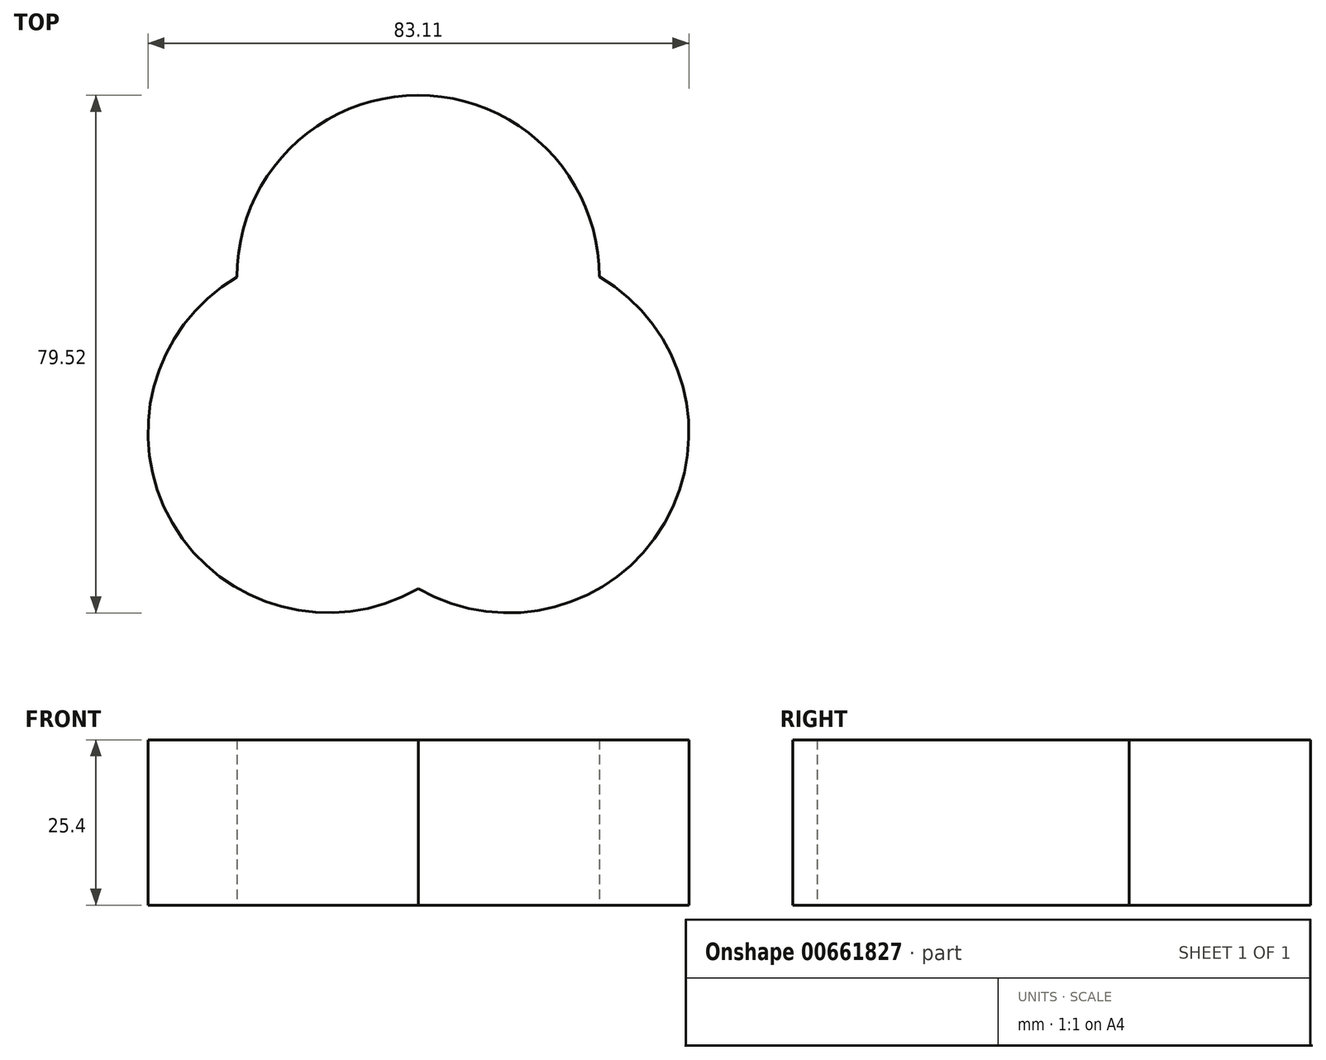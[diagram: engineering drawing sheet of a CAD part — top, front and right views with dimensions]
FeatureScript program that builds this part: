
annotation { "Feature Type Name" : "Feature", "Feature Type Description" : "" }
export const myFeature = defineFeature(function(context is Context, id is Id, definition is map)
    precondition{}
    {
        {
            var Q0;
            Q0=qCreatedBy(makeId("Top.planeOp"),FACE);
            var sketch = newSketch(context, id + "F0", { "sketchPlane" : qUnion([Q0])});
            skCircle(sketch, "E0", {"center": v(0, 0) * mm, "radius": 27.71 * mm});
            skCircle(sketch, "E1", {"center": v(-27.71, 0) * mm, "radius": 27.69 * mm});
            skCircle(sketch, "E2", {"center": v(-13.88, 23.99) * mm, "radius": 27.83 * mm});
            skSolve(sketch);
        }
        {
            var Q0;
            {var subQ0=sQuery(id+"F0.wireOp",EDGE,"E2");var subQ1=sQuery(id+"F0.wireOp",EDGE,"E0");var subQ2=makeQuery(id+"F0.imprint","INTERSECT",VERTEX,{"disambiguationData":[OD(0.0)],"derivedFrom":[subQ1,subQ0]});Q0=makeQuery(id+"F0.imprint","IMPRINT",FACE,{"disambiguationData":[TD([[makeQuery(id+"F0.imprint","IMPRINT",EDGE,{"disambiguationData":[TD([[subQ2,-1.0]])],"derivedFrom":subQ1}),-1.0]])]});}
            var Q1;
            {var subQ0=sQuery(id+"F0.wireOp",EDGE,"E1");var subQ1=sQuery(id+"F0.wireOp",EDGE,"E0");var subQ2=makeQuery(id+"F0.imprint","INTERSECT",VERTEX,{"disambiguationData":[OD(1.0)],"derivedFrom":[subQ1,subQ0]});Q1=makeQuery(id+"F0.imprint","IMPRINT",FACE,{"disambiguationData":[TD([[makeQuery(id+"F0.imprint","IMPRINT",EDGE,{"disambiguationData":[TD([[subQ2,-1.0]])],"derivedFrom":subQ1}),-1.0]])]});}
            var Q2;
            {var subQ0=sQuery(id+"F0.wireOp",EDGE,"E2");var subQ1=sQuery(id+"F0.wireOp",EDGE,"E0");var subQ2=makeQuery(id+"F0.imprint","INTERSECT",VERTEX,{"disambiguationData":[OD(0.0)],"derivedFrom":[subQ1,subQ0]});Q2=makeQuery(id+"F0.imprint","IMPRINT",FACE,{"disambiguationData":[TD([[makeQuery(id+"F0.imprint","IMPRINT",EDGE,{"disambiguationData":[TD([[subQ2,-1.0]])],"derivedFrom":subQ1}),1.0]])]});}
            var Q3;
            {var subQ0=sQuery(id+"F0.wireOp",EDGE,"E1");var subQ1=sQuery(id+"F0.wireOp",EDGE,"E0");var subQ2=makeQuery(id+"F0.imprint","INTERSECT",VERTEX,{"disambiguationData":[OD(1.0)],"derivedFrom":[subQ1,subQ0]});Q3=makeQuery(id+"F0.imprint","IMPRINT",FACE,{"disambiguationData":[TD([[makeQuery(id+"F0.imprint","IMPRINT",EDGE,{"disambiguationData":[TD([[subQ2,-1.0]])],"derivedFrom":subQ1}),1.0]])]});}
            var Q4;
            {var subQ0=sQuery(id+"F0.wireOp",EDGE,"E1");var subQ1=sQuery(id+"F0.wireOp",EDGE,"E0");var subQ2=makeQuery(id+"F0.imprint","INTERSECT",VERTEX,{"disambiguationData":[OD(0.0)],"derivedFrom":[subQ1,subQ0]});Q4=makeQuery(id+"F0.imprint","IMPRINT",FACE,{"disambiguationData":[TD([[makeQuery(id+"F0.imprint","IMPRINT",EDGE,{"disambiguationData":[TD([[subQ2,1.0]])],"derivedFrom":subQ1}),1.0]])]});}
            var Q5;
            {var subQ0=sQuery(id+"F0.wireOp",EDGE,"E2");var subQ1=sQuery(id+"F0.wireOp",EDGE,"E0");var subQ2=makeQuery(id+"F0.imprint","INTERSECT",VERTEX,{"disambiguationData":[OD(0.0)],"derivedFrom":[subQ1,subQ0]});Q5=makeQuery(id+"F0.imprint","IMPRINT",FACE,{"disambiguationData":[TD([[makeQuery(id+"F0.imprint","IMPRINT",EDGE,{"disambiguationData":[TD([[subQ2,1.0]])],"derivedFrom":subQ1}),1.0]])]});}
            var Q6;
            {var subQ0=sQuery(id+"F0.wireOp",EDGE,"E1");var subQ1=sQuery(id+"F0.wireOp",EDGE,"E0");var subQ2=makeQuery(id+"F0.imprint","INTERSECT",VERTEX,{"disambiguationData":[OD(0.0)],"derivedFrom":[subQ1,subQ0]});Q6=makeQuery(id+"F0.imprint","IMPRINT",FACE,{"disambiguationData":[TD([[makeQuery(id+"F0.imprint","IMPRINT",EDGE,{"disambiguationData":[TD([[subQ2,1.0]])],"derivedFrom":subQ1}),-1.0]])]});}
            extrude(context, id + "F1", {"entities" : qUnion([Q0, Q1, Q2, Q3, Q4, Q5, Q6]), "depth" : 25.4 * mm, "offsetDistance" : 25.4 * mm});
        }
    });
